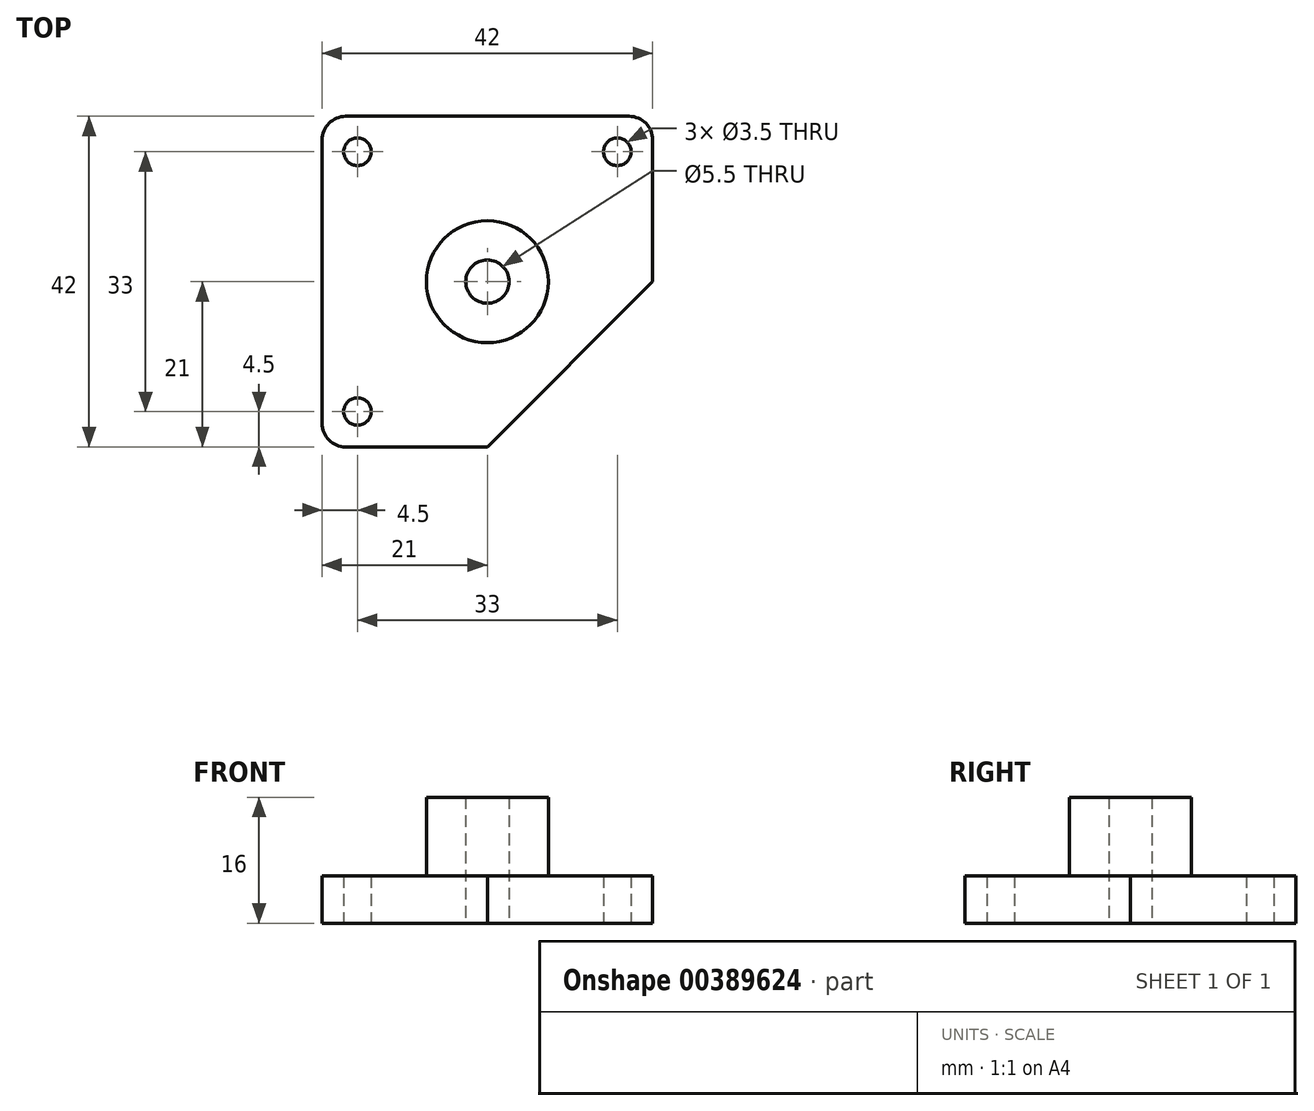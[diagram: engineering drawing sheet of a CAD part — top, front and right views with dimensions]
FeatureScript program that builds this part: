
annotation { "Feature Type Name" : "Feature", "Feature Type Description" : "" }
export const myFeature = defineFeature(function(context is Context, id is Id, definition is map)
    precondition{}
    {
        {
            var Q0;
            Q0=qCreatedBy(makeId("Top.planeOp"),FACE);
            var sketch = newSketch(context, id + "F0", { "sketchPlane" : qUnion([Q0])});
            skLineSegment(sketch, "E0.bottom", {"start": v(16.5, 16.5) * mm, "end": v(-16.5, 16.5) * mm, "construction": true});
            skLineSegment(sketch, "E0.top", {"start": v(16.5, -16.5) * mm, "end": v(-16.5, -16.5) * mm, "construction": true});
            skLineSegment(sketch, "E0.left", {"start": v(16.5, 16.5) * mm, "end": v(16.5, -16.5) * mm, "construction": true});
            skLineSegment(sketch, "E0.right", {"start": v(-16.5, 16.5) * mm, "end": v(-16.5, -16.5) * mm, "construction": true});
            skPoint(sketch, "E0.middle", {"position": v(0, 0) * mm});
            skCircle(sketch, "E1", {"center": v(-16.5, 16.5) * mm, "radius": 1.75 * mm});
            skCircle(sketch, "E2", {"center": v(16.5, 16.5) * mm, "radius": 1.75 * mm});
            skCircle(sketch, "E3", {"center": v(16.5, -16.5) * mm, "radius": 1.75 * mm});
            skCircle(sketch, "E4", {"center": v(-16.5, -16.5) * mm, "radius": 1.75 * mm});
            skLineSegment(sketch, "E5.bottom", {"start": v(18, 21) * mm, "end": v(-18, 21) * mm});
            skLineSegment(sketch, "E5.top", {"start": v(18, -21) * mm, "end": v(-18, -21) * mm});
            skLineSegment(sketch, "E5.left", {"start": v(21, 18) * mm, "end": v(21, -18) * mm});
            skLineSegment(sketch, "E5.right", {"start": v(-21, 18) * mm, "end": v(-21, -18) * mm});
            skPoint(sketch, "E6.visualSharp", {"position": v(-21, 21) * mm});
            skArc(sketch, "E6.filletArc", {"start": v(-18, 21) * mm, "mid": v(-20.12, 20.12) * mm, "end": v(-21, 18) * mm});
            skPoint(sketch, "E7.visualSharp", {"position": v(-21, -21) * mm});
            skArc(sketch, "E7.filletArc", {"start": v(-21, -18) * mm, "mid": v(-20.12, -20.12) * mm, "end": v(-18, -21) * mm});
            skPoint(sketch, "E8.visualSharp", {"position": v(21, -21) * mm});
            skArc(sketch, "E8.filletArc", {"start": v(18, -21) * mm, "mid": v(20.12, -20.12) * mm, "end": v(21, -18) * mm});
            skPoint(sketch, "E9.visualSharp", {"position": v(21, 21) * mm});
            skArc(sketch, "E9.filletArc", {"start": v(21, 18) * mm, "mid": v(20.12, 20.12) * mm, "end": v(18, 21) * mm});
            skCircle(sketch, "E10", {"center": v(0, 0) * mm, "radius": 2.75 * mm});
            skSolve(sketch);
        }
        {
            var Q0;
            Q0 = qSketchRegion(id + "F0", true);
            extrude(context, id + "F1", {"entities" : qUnion([Q0]), "depth" : 6 * mm});
        }
        {
            var Q0;
            Q0=makeQuery(id+"F1.opExtrude","CAP_FACE",FACE,{"disambiguationData":[OSD([sQuery(id+"F0.wireOp",EDGE,"E1"),sQuery(id+"F0.wireOp",EDGE,"E2"),sQuery(id+"F0.wireOp",EDGE,"E3"),sQuery(id+"F0.wireOp",EDGE,"E4"),sQuery(id+"F0.wireOp",EDGE,"E5.bottom"),sQuery(id+"F0.wireOp",EDGE,"E5.top"),sQuery(id+"F0.wireOp",EDGE,"E5.left"),sQuery(id+"F0.wireOp",EDGE,"E5.right"),sQuery(id+"F0.wireOp",EDGE,"E6.filletArc"),sQuery(id+"F0.wireOp",EDGE,"E7.filletArc"),sQuery(id+"F0.wireOp",EDGE,"E8.filletArc"),sQuery(id+"F0.wireOp",EDGE,"E9.filletArc"),sQuery(id+"F0.wireOp",EDGE,"E10")])],"isStart":false});
            var sketch = newSketch(context, id + "F2", { "sketchPlane" : qUnion([Q0])});
            skLineSegment(sketch, "E11", {"start": v(0, -21) * mm, "end": v(21, 0) * mm});
            skLineSegment(sketch, "E12", {"start": v(21, 0) * mm, "end": v(21, -21) * mm});
            skLineSegment(sketch, "E13", {"start": v(21, -21) * mm, "end": v(0, -21) * mm});
            skSolve(sketch);
        }
        {
            var Q0;
            Q0 = qSketchRegion(id + "F2", true);
            extrude(context, id + "F3", {"entities" : qUnion([Q0]), "operationType" : NewBodyOperationType.REMOVE, "oppositeDirection" : true, "depth" : 25 * mm});
        }
        {
            var Q0;
            Q0=makeQuery(id+"F1.opExtrude","CAP_FACE",FACE,{"disambiguationData":[OSD([sQuery(id+"F0.wireOp",EDGE,"E1"),sQuery(id+"F0.wireOp",EDGE,"E2"),sQuery(id+"F0.wireOp",EDGE,"E3"),sQuery(id+"F0.wireOp",EDGE,"E4"),sQuery(id+"F0.wireOp",EDGE,"E5.bottom"),sQuery(id+"F0.wireOp",EDGE,"E5.top"),sQuery(id+"F0.wireOp",EDGE,"E5.left"),sQuery(id+"F0.wireOp",EDGE,"E5.right"),sQuery(id+"F0.wireOp",EDGE,"E6.filletArc"),sQuery(id+"F0.wireOp",EDGE,"E7.filletArc"),sQuery(id+"F0.wireOp",EDGE,"E8.filletArc"),sQuery(id+"F0.wireOp",EDGE,"E9.filletArc"),sQuery(id+"F0.wireOp",EDGE,"E10")])],"isStart":false});
            var sketch = newSketch(context, id + "F4", { "sketchPlane" : qUnion([Q0])});
            skCircle(sketch, "E14.0", {"center": v(0, 0) * mm, "radius": 2.75 * mm});
            skCircle(sketch, "E15.0", {"center": v(0, 0) * mm, "radius": 7.75 * mm});
            skSolve(sketch);
        }
        {
            var Q0;
            Q0 = qSketchRegion(id + "F4", true);
            extrude(context, id + "F5", {"entities" : qUnion([Q0]), "operationType" : NewBodyOperationType.ADD, "depth" : 10 * mm});
        }
    });
